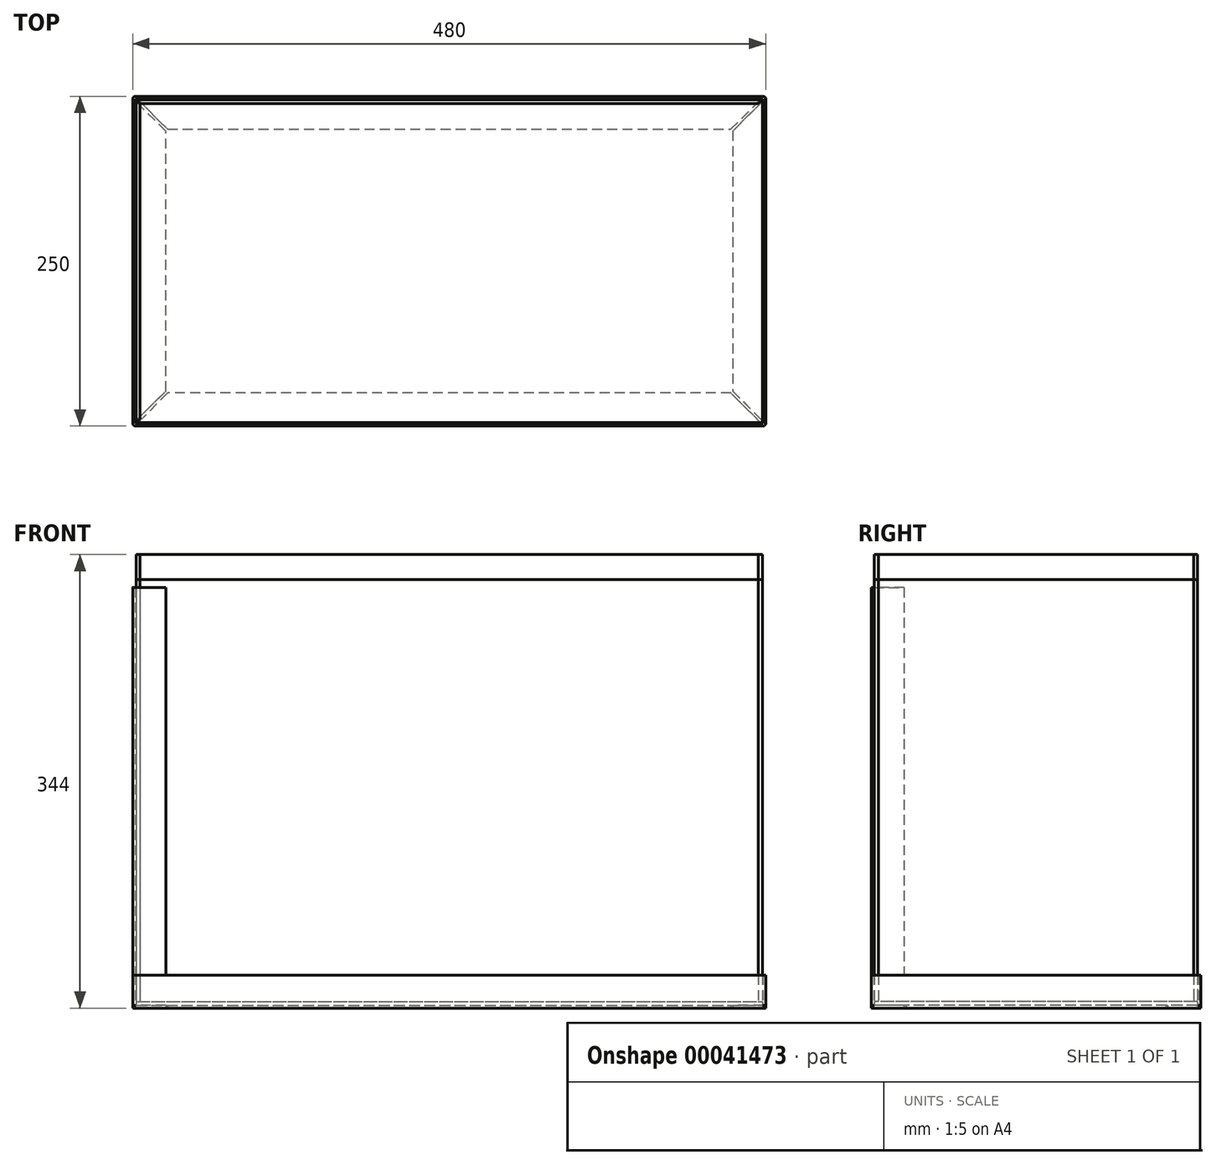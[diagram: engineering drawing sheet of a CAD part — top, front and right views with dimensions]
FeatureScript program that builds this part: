
annotation { "Feature Type Name" : "Feature", "Feature Type Description" : "" }
export const myFeature = defineFeature(function(context is Context, id is Id, definition is map)
    precondition{}
    {
        {
            var Q0;
            Q0=qCreatedBy(makeId("Top.planeOp"),FACE);
            var sketch = newSketch(context, id + "F0", { "sketchPlane" : qUnion([Q0])});
            skLineSegment(sketch, "E0", {"start": v(0, 125) * mm, "end": v(0, -125) * mm, "construction": true});
            skLineSegment(sketch, "E1", {"start": v(240, 0) * mm, "end": v(-240, 0) * mm, "construction": true});
            skLineSegment(sketch, "E2", {"start": v(-240, 123.59) * mm, "end": v(-238.59, 125) * mm, "construction": true});
            skLineSegment(sketch, "E3", {"start": v(-238.59, 125) * mm, "end": v(238.59, 125) * mm});
            skLineSegment(sketch, "E4", {"start": v(238.59, 125) * mm, "end": v(240, 123.59) * mm, "construction": true});
            skLineSegment(sketch, "E5", {"start": v(240, 123.59) * mm, "end": v(240, -123.59) * mm});
            skLineSegment(sketch, "E6", {"start": v(240, -123.59) * mm, "end": v(238.59, -125) * mm, "construction": true});
            skLineSegment(sketch, "E7", {"start": v(238.59, -125) * mm, "end": v(-238.59, -125) * mm});
            skLineSegment(sketch, "E8", {"start": v(-238.59, -125) * mm, "end": v(-240, -123.59) * mm, "construction": true});
            skLineSegment(sketch, "E9", {"start": v(-240, -123.59) * mm, "end": v(-240, 123.59) * mm});
            skLineSegment(sketch, "E10", {"start": v(-238.59, 125) * mm, "end": v(-213.59, 100) * mm});
            skLineSegment(sketch, "E11", {"start": v(-213.59, 100) * mm, "end": v(213.59, 100) * mm});
            skLineSegment(sketch, "E12", {"start": v(213.59, 100) * mm, "end": v(238.59, 125) * mm});
            skLineSegment(sketch, "E13", {"start": v(240, 123.59) * mm, "end": v(215, 98.59) * mm});
            skLineSegment(sketch, "E14", {"start": v(215, 98.59) * mm, "end": v(215, -98.59) * mm});
            skLineSegment(sketch, "E15", {"start": v(215, -98.59) * mm, "end": v(240, -123.59) * mm});
            skLineSegment(sketch, "E16", {"start": v(238.59, -125) * mm, "end": v(213.59, -100) * mm});
            skLineSegment(sketch, "E17", {"start": v(213.59, -100) * mm, "end": v(-213.59, -100) * mm});
            skLineSegment(sketch, "E18", {"start": v(-213.59, -100) * mm, "end": v(-238.59, -125) * mm});
            skLineSegment(sketch, "E19", {"start": v(-240, -123.59) * mm, "end": v(-215, -98.59) * mm});
            skLineSegment(sketch, "E20", {"start": v(-215, -98.59) * mm, "end": v(-215, 98.59) * mm});
            skLineSegment(sketch, "E21", {"start": v(-215, 98.59) * mm, "end": v(-240, 123.59) * mm});
            skSolve(sketch);
        }
        {
            var Q0;
            Q0 = qSketchRegion(id + "F0", true);
            extrude(context, id + "F1", {"entities" : qUnion([Q0]), "depth" : 2 * mm});
        }
        {
            var Q0;
            Q0=makeQuery(id+"F1.opExtrude","CAP_FACE",FACE,{"disambiguationData":[OSD([sQuery(id+"F0.wireOp",EDGE,"E9"),sQuery(id+"F0.wireOp",EDGE,"E19"),sQuery(id+"F0.wireOp",EDGE,"E20"),sQuery(id+"F0.wireOp",EDGE,"E21")])],"isStart":false});
            var sketch = newSketch(context, id + "F2", { "sketchPlane" : qUnion([Q0])});
            skSolve(sketch);
        }
        {
            var Q0;
            Q0=makeQuery(id+"F2.imprint","IMPRINT",FACE,{"disambiguationData":[TD([[makeQuery(id+"F2.imprint","IMPRINT",EDGE,{"derivedFrom":makeQuery(id+"F1.opExtrude","CAP_EDGE",EDGE,{"disambiguationData":[OSD([sQuery(id+"F0.wireOp",EDGE,"E9")])],"isStart":false})}),-1.0]])]});
            var sketch = newSketch(context, id + "F3", { "sketchPlane" : qUnion([Q0])});
            skLineSegment(sketch, "E22.bottom", {"start": v(-238, 125) * mm, "end": v(238, 125) * mm});
            skLineSegment(sketch, "E22.top", {"start": v(-238, -125) * mm, "end": v(238, -125) * mm});
            skLineSegment(sketch, "E22.left", {"start": v(-240, 123) * mm, "end": v(-240, -123) * mm});
            skLineSegment(sketch, "E22.right", {"start": v(240, 123) * mm, "end": v(240, -123) * mm});
            skLineSegment(sketch, "E23.0", {"start": v(238, 123) * mm, "end": v(238, -123) * mm});
            skLineSegment(sketch, "E23.1", {"start": v(-238, 123) * mm, "end": v(238, 123) * mm});
            skLineSegment(sketch, "E23.2", {"start": v(-238, 123) * mm, "end": v(-238, -123) * mm});
            skLineSegment(sketch, "E23.3", {"start": v(-238, -123) * mm, "end": v(238, -123) * mm});
            skPoint(sketch, "E24.visualSharp", {"position": v(240, 125) * mm});
            skArc(sketch, "E24.filletArc", {"start": v(240, 123) * mm, "mid": v(239.41, 124.41) * mm, "end": v(238, 125) * mm});
            skPoint(sketch, "E25.visualSharp", {"position": v(240, -125) * mm});
            skArc(sketch, "E25.filletArc", {"start": v(238, -125) * mm, "mid": v(239.41, -124.41) * mm, "end": v(240, -123) * mm});
            skPoint(sketch, "E26.visualSharp", {"position": v(-240, -125) * mm});
            skArc(sketch, "E26.filletArc", {"start": v(-240, -123) * mm, "mid": v(-239.41, -124.41) * mm, "end": v(-238, -125) * mm});
            skPoint(sketch, "E27.visualSharp", {"position": v(-240, 125) * mm});
            skArc(sketch, "E27.filletArc", {"start": v(-238, 125) * mm, "mid": v(-239.41, 124.41) * mm, "end": v(-240, 123) * mm});
            skSolve(sketch);
        }
        {
            var Q0;
            Q0 = qSketchRegion(id + "F3", true);
            extrude(context, id + "F4", {"entities" : qUnion([Q0]), "operationType" : NewBodyOperationType.ADD, "depth" : 23 * mm});
        }
        {
            var Q0;
            {var subQ0=sQuery(id+"F0.wireOp",EDGE,"E13");var subQ1=sQuery(id+"F0.wireOp",EDGE,"E14");var subQ2=sQuery(id+"F0.wireOp",EDGE,"E15");Q0=makeQuery(id+"F4.boolean.opBoolean","SPLIT",FACE,{"disambiguationData":[TD([makeQuery(id+"F1.opExtrude","SWEPT_FACE",FACE,{"disambiguationData":[OSD([subQ1])]})])],"derivedFrom":makeQuery(id+"F1.opExtrude","CAP_FACE",FACE,{"disambiguationData":[OSD([sQuery(id+"F0.wireOp",EDGE,"E5"),subQ0,subQ1,subQ2])],"isStart":false})});}
            var sketch = newSketch(context, id + "F5", { "sketchPlane" : qUnion([Q0])});
            skLineSegment(sketch, "E28.0", {"start": v(-237.5, 122.5) * mm, "end": v(-237.5, -122.5) * mm});
            skLineSegment(sketch, "E28.1", {"start": v(-237.5, 122.5) * mm, "end": v(237.5, 122.5) * mm});
            skLineSegment(sketch, "E28.2", {"start": v(237.5, 122.5) * mm, "end": v(237.5, -122.5) * mm});
            skLineSegment(sketch, "E28.3", {"start": v(-237.5, -122.5) * mm, "end": v(237.5, -122.5) * mm});
            skSolve(sketch);
        }
        {
            var Q0;
            Q0 = qSketchRegion(id + "F5", true);
            extrude(context, id + "F6", {"entities" : qUnion([Q0]), "depth" : 3 * mm});
        }
        {
            var Q0;
            Q0 = qSketchRegion(id + "F3", true);
            extrude(context, id + "F7", {"entities" : qUnion([Q0]), "depth" : 25 * mm});
        }
        {
            var Q0;
            Q0=makeQuery(id+"F7.opExtrude","SWEPT_BODY",BODY,{"disambiguationData":[OSD([sQuery(id+"F3.wireOp",EDGE,"E22.bottom"),sQuery(id+"F3.wireOp",EDGE,"E22.top"),sQuery(id+"F3.wireOp",EDGE,"E22.left"),sQuery(id+"F3.wireOp",EDGE,"E22.right"),sQuery(id+"F3.wireOp",EDGE,"E23.0"),sQuery(id+"F3.wireOp",EDGE,"E23.1"),sQuery(id+"F3.wireOp",EDGE,"E23.2"),sQuery(id+"F3.wireOp",EDGE,"E23.3"),sQuery(id+"F3.wireOp",EDGE,"E24.filletArc"),sQuery(id+"F3.wireOp",EDGE,"E25.filletArc"),sQuery(id+"F3.wireOp",EDGE,"E26.filletArc"),sQuery(id+"F3.wireOp",EDGE,"E27.filletArc")])]});
            deleteBodies(context, id + "F8", {"entities" : qUnion([Q0])});
        }
        {
            var Q0;
            Q0=makeQuery(id+"F6.opExtrude","CAP_FACE",FACE,{"disambiguationData":[OSD([sQuery(id+"F5.wireOp",EDGE,"E28.0"),sQuery(id+"F5.wireOp",EDGE,"E28.1"),sQuery(id+"F5.wireOp",EDGE,"E28.2"),sQuery(id+"F5.wireOp",EDGE,"E28.3")])],"isStart":false});
            var sketch = newSketch(context, id + "F9", { "sketchPlane" : qUnion([Q0])});
            skLineSegment(sketch, "E29.0", {"start": v(-237.5, 122.5) * mm, "end": v(237.5, 122.5) * mm});
            skLineSegment(sketch, "E30", {"start": v(-237.5, 122.5) * mm, "end": v(-234.5, 119.5) * mm});
            skLineSegment(sketch, "E31", {"start": v(-234.5, 119.5) * mm, "end": v(234.5, 119.5) * mm});
            skLineSegment(sketch, "E32", {"start": v(234.5, 119.5) * mm, "end": v(237.5, 122.5) * mm});
            skSolve(sketch);
        }
        {
            var Q0;
            Q0 = qSketchRegion(id + "F9", true);
            extrude(context, id + "F10", {"entities" : qUnion([Q0]), "depth" : 320 * mm});
        }
        {
            var Q0;
            Q0=makeQuery(id+"F6.opExtrude","CAP_FACE",FACE,{"disambiguationData":[OSD([sQuery(id+"F5.wireOp",EDGE,"E28.0"),sQuery(id+"F5.wireOp",EDGE,"E28.1"),sQuery(id+"F5.wireOp",EDGE,"E28.2"),sQuery(id+"F5.wireOp",EDGE,"E28.3")])],"isStart":false});
            var sketch = newSketch(context, id + "F11", { "sketchPlane" : qUnion([Q0])});
            skLineSegment(sketch, "E33.0", {"start": v(-237.5, 122.5) * mm, "end": v(-237.5, -122.5) * mm});
            skLineSegment(sketch, "E34.1", {"start": v(-237.5, 122.5) * mm, "end": v(-234.5, 119.5) * mm});
            skLineSegment(sketch, "E35", {"start": v(-234.5, 119.5) * mm, "end": v(-234.5, -119.5) * mm});
            skLineSegment(sketch, "E36", {"start": v(-234.5, -119.5) * mm, "end": v(-237.5, -122.5) * mm});
            skSolve(sketch);
        }
        {
            var Q0;
            Q0 = qSketchRegion(id + "F11", true);
            var Q1;
            Q1=makeQuery(id+"F10.opExtrude","CAP_FACE",FACE,{"disambiguationData":[OSD([sQuery(id+"F9.wireOp",EDGE,"E29.0"),sQuery(id+"F9.wireOp",EDGE,"E30"),sQuery(id+"F9.wireOp",EDGE,"E31"),sQuery(id+"F9.wireOp",EDGE,"E32")])],"isStart":false});
            extrude(context, id + "F12", {"entities" : qUnion([Q0]), "endBound" : BoundingType.UP_TO_SURFACE, "endBoundEntityFace" : qUnion([Q1]), "depth" : 25 * mm});
        }
        {
            var Q0;
            Q0=makeQuery(id+"F4.opExtrude","CAP_FACE",FACE,{"disambiguationData":[OSD([sQuery(id+"F3.wireOp",EDGE,"E22.bottom"),sQuery(id+"F3.wireOp",EDGE,"E22.top"),sQuery(id+"F3.wireOp",EDGE,"E22.left"),sQuery(id+"F3.wireOp",EDGE,"E22.right"),sQuery(id+"F3.wireOp",EDGE,"E23.0"),sQuery(id+"F3.wireOp",EDGE,"E23.1"),sQuery(id+"F3.wireOp",EDGE,"E23.2"),sQuery(id+"F3.wireOp",EDGE,"E23.3"),sQuery(id+"F3.wireOp",EDGE,"E24.filletArc"),sQuery(id+"F3.wireOp",EDGE,"E25.filletArc"),sQuery(id+"F3.wireOp",EDGE,"E26.filletArc"),sQuery(id+"F3.wireOp",EDGE,"E27.filletArc")])],"isStart":false});
            var sketch = newSketch(context, id + "F13", { "sketchPlane" : qUnion([Q0])});
            skArc(sketch, "E37.0", {"start": v(-240, -123) * mm, "mid": v(-239.41, -124.41) * mm, "end": v(-238, -125) * mm});
            skLineSegment(sketch, "E37.1", {"start": v(-238, -125) * mm, "end": v(-215, -125) * mm});
            skLineSegment(sketch, "E37.2", {"start": v(-240, -123) * mm, "end": v(-240, -100) * mm});
            skLineSegment(sketch, "E37.3", {"start": v(-238, -100) * mm, "end": v(-238, -123) * mm});
            skLineSegment(sketch, "E37.4", {"start": v(-238, -123) * mm, "end": v(-215, -123) * mm});
            skLineSegment(sketch, "E38", {"start": v(-240, -100) * mm, "end": v(-238, -100) * mm});
            skLineSegment(sketch, "E39", {"start": v(-215, -123) * mm, "end": v(-215, -125) * mm});
            skPoint(sketch, "E40.orphan", {"position": v(-238, 123) * mm});
            skPoint(sketch, "E41.orphan", {"position": v(-240, 123) * mm});
            skPoint(sketch, "E42.orphan", {"position": v(238, -125) * mm});
            skPoint(sketch, "E43.orphan", {"position": v(238, -123) * mm});
            skSolve(sketch);
        }
        {
            var Q0;
            Q0 = qSketchRegion(id + "F13", true);
            extrude(context, id + "F14", {"entities" : qUnion([Q0]), "depth" : 294 * mm});
        }
        {
            var Q0;
            Q0=makeQuery(id+"F10.opExtrude","CAP_FACE",FACE,{"disambiguationData":[OSD([sQuery(id+"F9.wireOp",EDGE,"E29.0"),sQuery(id+"F9.wireOp",EDGE,"E30"),sQuery(id+"F9.wireOp",EDGE,"E31"),sQuery(id+"F9.wireOp",EDGE,"E32")])],"isStart":false});
            var sketch = newSketch(context, id + "F15", { "sketchPlane" : qUnion([Q0])});
            skLineSegment(sketch, "E44.0.0", {"start": v(237.5, 122.5) * mm, "end": v(-237.5, 122.5) * mm});
            skLineSegment(sketch, "E44.0.1", {"start": v(-237.5, 122.5) * mm, "end": v(-234.5, 119.5) * mm});
            skLineSegment(sketch, "E44.0.2", {"start": v(-234.5, 119.5) * mm, "end": v(234.5, 119.5) * mm});
            skLineSegment(sketch, "E44.0.3", {"start": v(234.5, 119.5) * mm, "end": v(237.5, 122.5) * mm});
            skSolve(sketch);
        }
        {
            var Q0;
            Q0 = qSketchRegion(id + "F15", true);
            extrude(context, id + "F16", {"entities" : qUnion([Q0]), "depth" : 19 * mm});
        }
        {
            var Q0;
            Q0=makeQuery(id+"F12.opExtrude","CAP_FACE",FACE,{"disambiguationData":[OSD([sQuery(id+"F11.wireOp",EDGE,"E33.0"),sQuery(id+"F11.wireOp",EDGE,"E34.1"),sQuery(id+"F11.wireOp",EDGE,"E35"),sQuery(id+"F11.wireOp",EDGE,"E36")])],"isStart":false});
            var sketch = newSketch(context, id + "F17", { "sketchPlane" : qUnion([Q0])});
            skLineSegment(sketch, "E45.0.0", {"start": v(-234.5, 119.5) * mm, "end": v(-237.5, 122.5) * mm});
            skLineSegment(sketch, "E45.0.1", {"start": v(-237.5, 122.5) * mm, "end": v(-237.5, -122.5) * mm});
            skLineSegment(sketch, "E45.0.2", {"start": v(-237.5, -122.5) * mm, "end": v(-234.5, -119.5) * mm});
            skLineSegment(sketch, "E45.0.3", {"start": v(-234.5, -119.5) * mm, "end": v(-234.5, 119.5) * mm});
            skSolve(sketch);
        }
        {
            var Q0;
            Q0 = qSketchRegion(id + "F17", true);
            extrude(context, id + "F18", {"entities" : qUnion([Q0]), "depth" : 19 * mm});
        }
    });
